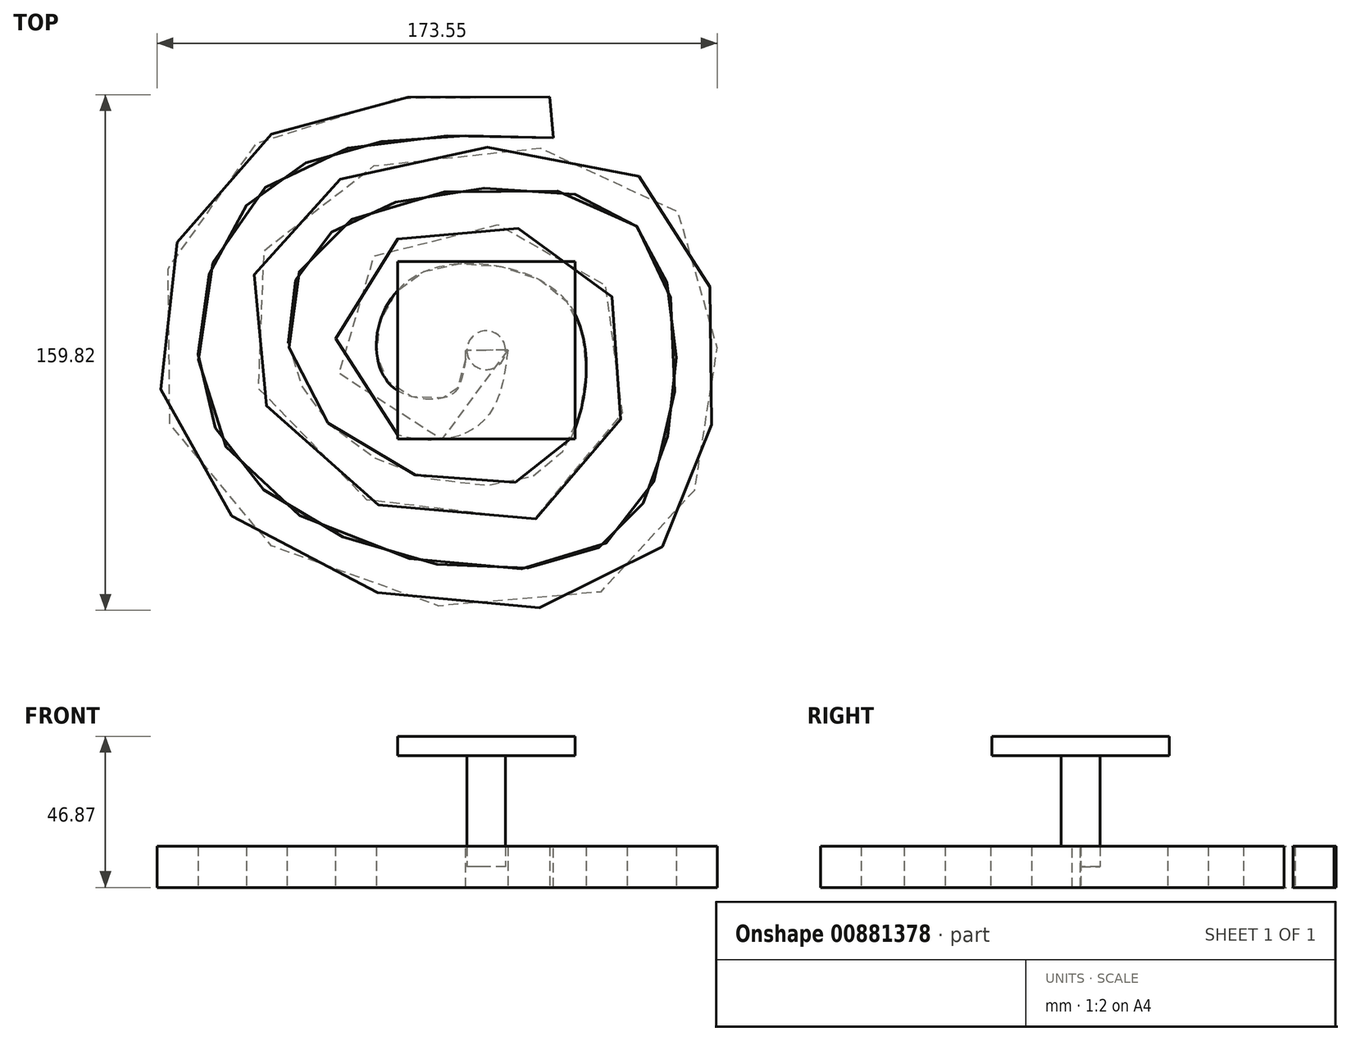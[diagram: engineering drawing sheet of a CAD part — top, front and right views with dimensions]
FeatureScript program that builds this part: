
annotation { "Feature Type Name" : "Feature", "Feature Type Description" : "" }
export const myFeature = defineFeature(function(context is Context, id is Id, definition is map)
    precondition{}
    {
        {
            var Q0;
            Q0=qCreatedBy(makeId("Front.planeOp"),FACE);
            var sketch = newSketch(context, id + "F0", { "sketchPlane" : qUnion([Q0])});
            skCircle(sketch, "E0.cCircle", {"center": v(0, 0) * mm, "radius": 6.37 * mm, "construction": true});
            skLineSegment(sketch, "E0.0", {"start": v(6.37, 6.37) * mm, "end": v(6.37, -6.37) * mm});
            skLineSegment(sketch, "E0.1", {"start": v(6.37, -6.37) * mm, "end": v(-6.37, -6.37) * mm});
            skLineSegment(sketch, "E0.2", {"start": v(-6.37, -6.37) * mm, "end": v(-6.37, 6.37) * mm});
            skLineSegment(sketch, "E0.3", {"start": v(-6.37, 6.37) * mm, "end": v(6.37, 6.37) * mm});
            skPoint(sketch, "E0.0.midPoint", {"position": v(6.37, 0) * mm});
            skSolve(sketch);
        }
        {
            var Q0;
            Q0=makeQuery(id+"F0.imprint","IMPRINT",FACE,{"disambiguationData":[TD([[makeQuery(id+"F0.imprint","IMPRINT",EDGE,{"derivedFrom":sQuery(id+"F0.wireOp",EDGE,"E0.0")}),-1.0]])]});
            extrude(context, id + "F1", {"entities" : qUnion([Q0]), "depth" : 2.6 * mm, "offsetDistance" : 25 * mm});
        }
        {
            var Q0;
            Q0=qCreatedBy(makeId("Top.planeOp"),FACE);
            var sketch = newSketch(context, id + "F2", { "sketchPlane" : qUnion([Q0])});
            skFitSpline(sketch, "E1", {"points": [v(0, 0) * mm, v(-7.22, -18.55) * mm, v(-31.3, -17.14) * mm, v(-39.8, 5.24) * mm, v(-25.07, 28.19) * mm, v(6.94, 31.58) * mm, v(31.3, 16.57) * mm, v(36.12, -15.44) * mm, v(16.85, -44.62) * mm, v(-39.52, -37.53) * mm, v(-67, 0) * mm, v(-58.21, 34.98) * mm, v(-18.55, 54.25) * mm, v(42.35, 49.15) * mm, v(63.03, 17.14) * mm, v(61.33, -31.3) * mm, v(40.93, -64.44) * mm, v(-11.76, -72.94) * mm, v(-75.78, -45.18) * mm, v(-95.32, 0) * mm, v(-78.33, 49.43) * mm, v(-34.98, 70.4) * mm, v(20.25, 71.8) * mm], "startDerivative": vector(-88.4, -704.81) * mm, "endDerivative": vector(1061.85, -44.5) * mm});
            skSolve(sketch);
        }
        {
            var Q0;
            Q0=makeQuery(id+"F1.opExtrude","CAP_FACE",FACE,{"disambiguationData":[OSD([sQuery(id+"F0.wireOp",EDGE,"E0.0"),sQuery(id+"F0.wireOp",EDGE,"E0.1"),sQuery(id+"F0.wireOp",EDGE,"E0.2"),sQuery(id+"F0.wireOp",EDGE,"E0.3")])],"isStart":false});
            var Q1;
            Q1=sQuery(id+"F2.wireOp",EDGE,"E1");
            sweep(context, id + "F3", {"operationType" : NewBodyOperationType.ADD, "profiles" : qUnion([Q0]), "path" : qUnion([Q1])});
        }
        {
            var Q0;
            Q0=qCreatedBy(makeId("Top.planeOp"),FACE);
            var sketch = newSketch(context, id + "F4", { "sketchPlane" : qUnion([Q0])});
            skCircle(sketch, "E2", {"center": v(0, 0) * mm, "radius": 6 * mm});
            skSolve(sketch);
        }
        {
            var Q0;
            Q0 = qSketchRegion(id + "F4", true);
            extrude(context, id + "F5", {"entities" : qUnion([Q0]), "operationType" : NewBodyOperationType.ADD, "depth" : 34.5 * mm, "offsetDistance" : 25 * mm});
        }
        {
            var Q0;
            Q0=makeQuery(id+"F5.opExtrude","CAP_FACE",FACE,{"disambiguationData":[OSD([sQuery(id+"F4.wireOp",EDGE,"E2")])],"isStart":false});
            var sketch = newSketch(context, id + "F6", { "sketchPlane" : qUnion([Q0])});
            skLineSegment(sketch, "E3.bottom", {"start": v(27.5, 27.5) * mm, "end": v(-27.5, 27.5) * mm});
            skLineSegment(sketch, "E3.top", {"start": v(27.5, -27.5) * mm, "end": v(-27.5, -27.5) * mm});
            skLineSegment(sketch, "E3.left", {"start": v(27.5, 27.5) * mm, "end": v(27.5, -27.5) * mm});
            skLineSegment(sketch, "E3.right", {"start": v(-27.5, 27.5) * mm, "end": v(-27.5, -27.5) * mm});
            skPoint(sketch, "E3.middle", {"position": v(0, 0) * mm});
            skSolve(sketch);
        }
        {
            var Q0;
            Q0=makeQuery(id+"F6.imprint","IMPRINT",FACE,{"disambiguationData":[TD([[makeQuery(id+"F6.imprint","IMPRINT",EDGE,{"derivedFrom":sQuery(id+"F6.wireOp",EDGE,"E3.bottom")}),1.0]])]});
            var Q1;
            Q1=makeQuery(id+"F6.imprint","IMPRINT",FACE,{"disambiguationData":[TD([[makeQuery(id+"F6.imprint","IMPRINT",EDGE,{"derivedFrom":makeQuery(id+"F5.opExtrude","CAP_EDGE",EDGE,{"disambiguationData":[OSD([sQuery(id+"F4.wireOp",EDGE,"E2")])],"isStart":false})}),1.0]])]});
            extrude(context, id + "F7", {"entities" : qUnion([Q0, Q1]), "operationType" : NewBodyOperationType.ADD, "depth" : 6 * mm, "offsetDistance" : 25 * mm});
        }
    });
